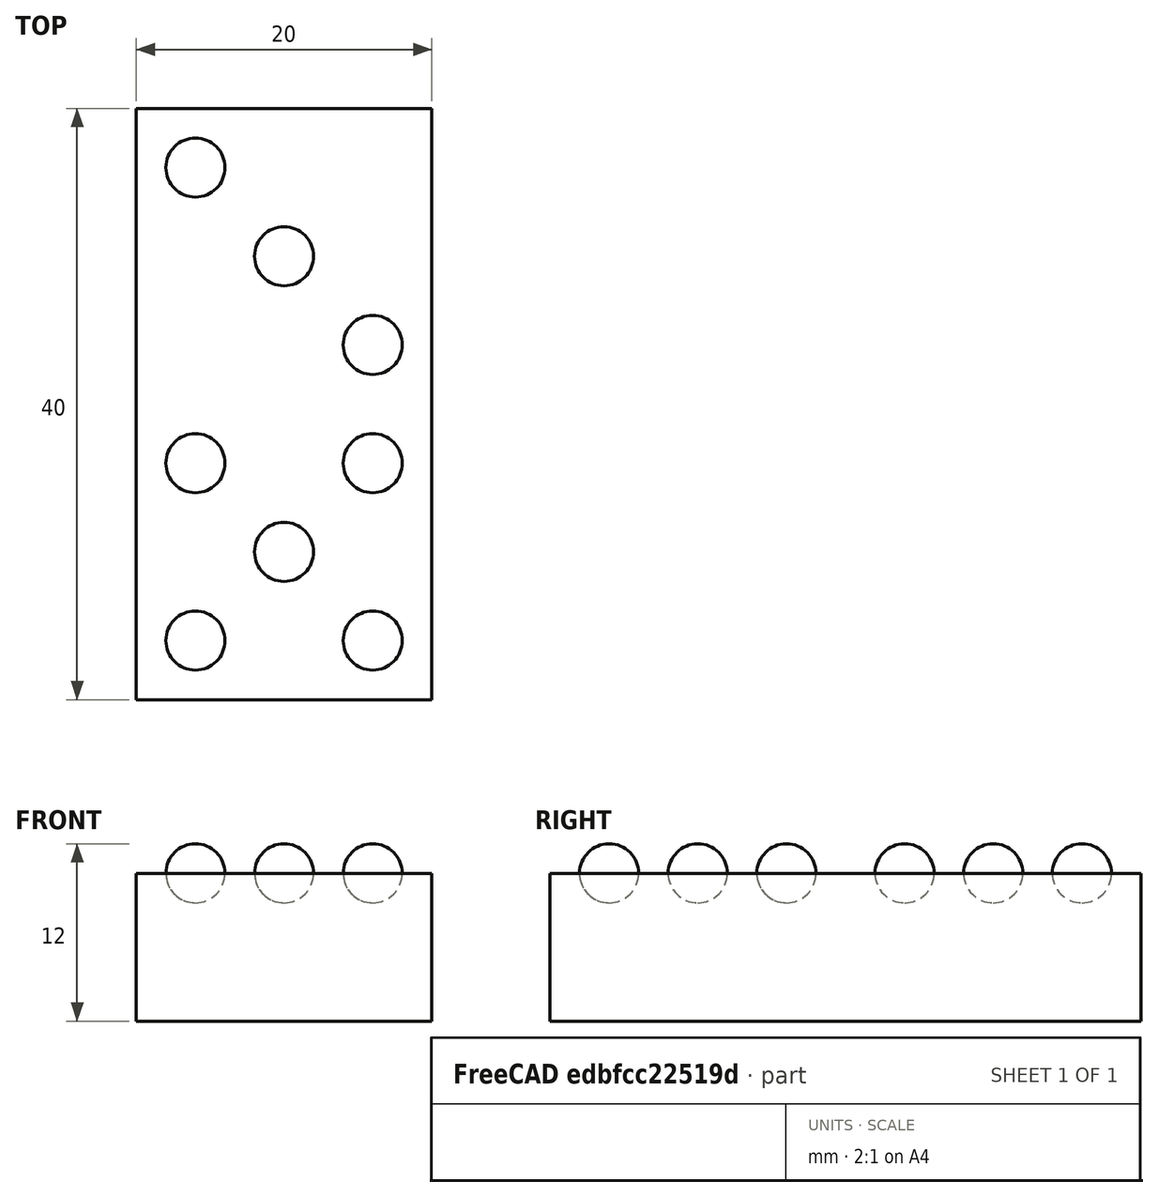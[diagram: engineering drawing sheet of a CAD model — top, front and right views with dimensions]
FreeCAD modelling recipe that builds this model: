
FCSTD DOCUMENT  (FreeCAD 0.20R29603 (Git))
Label: OJT1_T04R10_dichadominos
License: All rights reserved
LicenseURL: http://en.wikipedia.org/wiki/All_rights_reserved
objects: Part::Sphere×8, Part::MultiFuse×3, Part::Box×1, Part::Cut×1, Part::FeaturePython×1
note: 14 computed .brp shape members not serialized (recipe doc carries the construction recipe); baked Part::Feature solids carry a one-line shape summary decoded from their .brp

FEATURE [Part::Box] Box  label="Ficha-base"
  AttacherType = Attacher::AttachEngine3D
  Height = 10
  Length = 20
  Width = 40
FEATURE [Part::Sphere] Sphere  label="Esfera008"
  Angle1 = -90
  Angle2 = 90
  Angle3 = 360
  AttacherType = Attacher::AttachEngine3D
  Placement = pos=(4,4,10) rot=(0,0,1;0rad)
  Radius = 2
FEATURE [Part::Sphere] Sphere001  label="Esfera007"
  Angle1 = -90
  Angle2 = 90
  Angle3 = 360
  AttacherType = Attacher::AttachEngine3D
  Placement = pos=(4,16,10) rot=(0,0,1;0rad)
  Radius = 2
FEATURE [Part::Sphere] Sphere002  label="Esfera006"
  Angle1 = -90
  Angle2 = 90
  Angle3 = 360
  AttacherType = Attacher::AttachEngine3D
  Placement = pos=(10,10,10) rot=(0,0,1;0rad)
  Radius = 2
FEATURE [Part::Sphere] Sphere003  label="Esfera005"
  Angle1 = -90
  Angle2 = 90
  Angle3 = 360
  AttacherType = Attacher::AttachEngine3D
  Placement = pos=(16,16,10) rot=(0,0,1;0rad)
  Radius = 2
FEATURE [Part::Sphere] Sphere004  label="Esfera004"
  Angle1 = -90
  Angle2 = 90
  Angle3 = 360
  AttacherType = Attacher::AttachEngine3D
  Placement = pos=(16,4,10) rot=(0,0,1;0rad)
  Radius = 2
FEATURE [Part::MultiFuse] Fusion  label="Cara-5"
  Shapes = -> [Sphere,Sphere001,Sphere002,Sphere003,Sphere004]
FEATURE [Part::Sphere] Sphere005  label="Esfera003"
  Angle1 = -90
  Angle2 = 90
  Angle3 = 360
  AttacherType = Attacher::AttachEngine3D
  Placement = pos=(4,36,10) rot=(0,0,1;0rad)
  Radius = 2
FEATURE [Part::Sphere] Sphere006  label="Esfera002"
  Angle1 = -90
  Angle2 = 90
  Angle3 = 360
  AttacherType = Attacher::AttachEngine3D
  Placement = pos=(16,24,10) rot=(0,0,1;0rad)
  Radius = 2
FEATURE [Part::Sphere] Sphere007  label="Esfera"
  Angle1 = -90
  Angle2 = 90
  Angle3 = 360
  AttacherType = Attacher::AttachEngine3D
  Placement = pos=(10,30,10) rot=(0,0,1;0rad)
  Radius = 2
FEATURE [Part::MultiFuse] Fusion001  label="Cara-3"
  Shapes = -> [Sphere005,Sphere006,Sphere007]
FEATURE [Part::MultiFuse] Fusion002  label="Unió"
  Shapes = -> [Fusion,Fusion001]
FEATURE [Part::Cut] Cut  label="Ficha-5-3"
  Base = -> Box
  Tool = -> Fusion002
FEATURE [Part::FeaturePython] BooleanFragments  # WARN: FeaturePython — macro-defined, semantics opaque (R4)
  Mode = 0
  Objects = -> [Fusion002]
  Tolerance = 0
